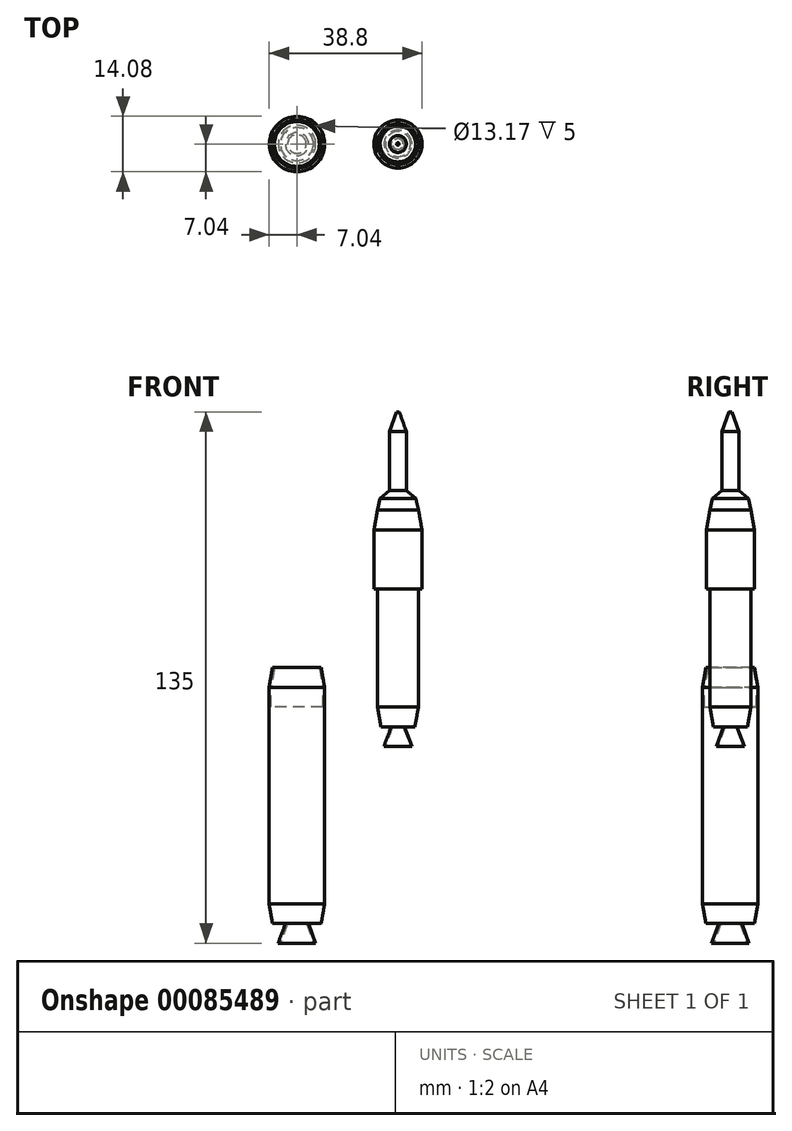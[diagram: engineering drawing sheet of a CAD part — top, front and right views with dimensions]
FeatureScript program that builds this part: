
annotation { "Feature Type Name" : "Feature", "Feature Type Description" : "" }
export const myFeature = defineFeature(function(context is Context, id is Id, definition is map)
    precondition{}
    {
        {
            var Q0;
            Q0=qCreatedBy(makeId("Top.planeOp"),FACE);
            var sketch = newSketch(context, id + "F0", { "sketchPlane" : qUnion([Q0])});
            skCircle(sketch, "E0", {"center": v(0, 0) * mm, "radius": 7.04 * mm});
            skSolve(sketch);
        }
        {
            var Q0;
            Q0=makeQuery(id+"F0.imprint","IMPRINT",FACE,{"disambiguationData":[TD([[makeQuery(id+"F0.imprint","IMPRINT",EDGE,{"derivedFrom":sQuery(id+"F0.wireOp",EDGE,"E0")}),1.0]])]});
            extrude(context, id + "F1", {"entities" : qUnion([Q0]), "depth" : 5 * mm, "hasSecondDirection" : true, "secondDirectionOppositeDirection" : true, "secondDirectionDepth" : 50 * mm});
        }
        {
            var Q0;
            Q0=makeQuery(id+"F1.opExtrude","CAP_FACE",FACE,{"disambiguationData":[OSD([sQuery(id+"F0.wireOp",EDGE,"E0")])],"isStart":true});
            extrude(context, id + "F2", {"entities" : qUnion([Q0]), "operationType" : NewBodyOperationType.ADD, "depth" : 5 * mm, "hasDraft" : true, "draftAngle" : 10 * degree, "draftPullDirection" : true});
        }
        {
            var Q0;
            Q0=makeQuery(id+"F1.opExtrude","CAP_FACE",FACE,{"disambiguationData":[OSD([sQuery(id+"F0.wireOp",EDGE,"E0")])],"isStart":false});
            extrude(context, id + "F3", {"entities" : qUnion([Q0]), "operationType" : NewBodyOperationType.ADD, "depth" : 5 * mm, "hasDraft" : true, "draftAngle" : 10 * degree, "draftPullDirection" : true});
        }
        {
            var Q0;
            Q0=makeQuery(id+"F3.opExtrude","CAP_FACE",FACE,{"disambiguationData":[OSD([sQuery(id+"F0.wireOp",EDGE,"E0")])],"isStart":false});
            var sketch = newSketch(context, id + "F4", { "sketchPlane" : qUnion([Q0])});
            skCircle(sketch, "E1", {"center": v(0, 0) * mm, "radius": 5.7 * mm});
            skSolve(sketch);
        }
        {
            var Q0;
            Q0 = qSketchRegion(id + "F4", true);
            extrude(context, id + "F5", {"entities" : qUnion([Q0]), "operationType" : NewBodyOperationType.REMOVE, "oppositeDirection" : true, "depth" : 5 * mm, "hasDraft" : true, "draftAngle" : 10 * degree});
        }
        {
            var Q0;
            Q0=makeQuery(id+"F2.opExtrude","CAP_FACE",FACE,{"disambiguationData":[OSD([sQuery(id+"F0.wireOp",EDGE,"E0")])],"isStart":false});
            var sketch = newSketch(context, id + "F6", { "sketchPlane" : qUnion([Q0])});
            skCircle(sketch, "E2", {"center": v(0, 0) * mm, "radius": 2.94 * mm});
            skSolve(sketch);
        }
        {
            var Q0;
            Q0 = qSketchRegion(id + "F6", true);
            extrude(context, id + "F7", {"entities" : qUnion([Q0]), "operationType" : NewBodyOperationType.ADD, "depth" : 5 * mm, "hasDraft" : true, "draftAngle" : 20 * degree});
        }
        {
            var Q0;
            Q0=makeQuery(id+"F7.opExtrude","CAP_FACE",FACE,{"disambiguationData":[OSD([sQuery(id+"F6.wireOp",EDGE,"E2")])],"isStart":false});
            var sketch = newSketch(context, id + "F8", { "sketchPlane" : qUnion([Q0])});
            skCircle(sketch, "E3", {"center": v(0, 0) * mm, "radius": 4.2 * mm});
            skSolve(sketch);
        }
        {
            var Q0;
            Q0 = qSketchRegion(id + "F8", true);
            extrude(context, id + "F9", {"entities" : qUnion([Q0]), "operationType" : NewBodyOperationType.REMOVE, "oppositeDirection" : true, "depth" : 5 * mm, "hasDraft" : true, "draftAngle" : 20 * degree, "draftPullDirection" : true});
        }
        {
            var Q0;
            Q0=qCreatedBy(makeId("Top.planeOp"),FACE);
            var sketch = newSketch(context, id + "F10", { "sketchPlane" : qUnion([Q0])});
            skCircle(sketch, "E4", {"center": v(25.65, 0) * mm, "radius": 5.21 * mm});
            skSolve(sketch);
        }
        {
            var Q0;
            Q0=makeQuery(id+"F10.imprint","IMPRINT",FACE,{"disambiguationData":[TD([[makeQuery(id+"F10.imprint","IMPRINT",EDGE,{"derivedFrom":sQuery(id+"F10.wireOp",EDGE,"E4")}),1.0]])]});
            extrude(context, id + "F11", {"entities" : qUnion([Q0]), "depth" : 30 * mm});
        }
        {
            var Q0;
            Q0=makeQuery(id+"F11.opExtrude","CAP_FACE",FACE,{"disambiguationData":[OSD([sQuery(id+"F10.wireOp",EDGE,"E4")])],"isStart":true});
            extrude(context, id + "F12", {"entities" : qUnion([Q0]), "operationType" : NewBodyOperationType.ADD, "depth" : 5 * mm, "hasDraft" : true, "draftAngle" : 10 * degree, "draftPullDirection" : true});
        }
        {
            var Q0;
            Q0=makeQuery(id+"F12.opExtrude","CAP_FACE",FACE,{"disambiguationData":[OSD([sQuery(id+"F10.wireOp",EDGE,"E4")])],"isStart":false});
            var sketch = newSketch(context, id + "F13", { "sketchPlane" : qUnion([Q0])});
            skCircle(sketch, "E5", {"center": v(25.65, 0) * mm, "radius": 1.72 * mm});
            skSolve(sketch);
        }
        {
            var Q0;
            Q0 = qSketchRegion(id + "F13", true);
            extrude(context, id + "F14", {"entities" : qUnion([Q0]), "operationType" : NewBodyOperationType.ADD, "depth" : 5 * mm, "hasDraft" : true, "draftAngle" : 20 * degree});
        }
        {
            var Q0;
            Q0=makeQuery(id+"F14.opExtrude","CAP_FACE",FACE,{"disambiguationData":[OSD([sQuery(id+"F13.wireOp",EDGE,"E5")])],"isStart":false});
            var sketch = newSketch(context, id + "F15", { "sketchPlane" : qUnion([Q0])});
            skCircle(sketch, "E6", {"center": v(25.65, 0) * mm, "radius": 3.17 * mm});
            skSolve(sketch);
        }
        {
            var Q0;
            Q0 = qSketchRegion(id + "F15", true);
            extrude(context, id + "F16", {"entities" : qUnion([Q0]), "operationType" : NewBodyOperationType.REMOVE, "oppositeDirection" : true, "depth" : 5 * mm, "hasDraft" : true, "draftAngle" : 20 * degree, "draftPullDirection" : true});
        }
        {
            var Q0;
            Q0=makeQuery(id+"F5.boolean.opBoolean","COPY",FACE,{"derivedFrom":makeQuery(id+"F5.opExtrude","CAP_FACE",FACE,{"disambiguationData":[OSD([sQuery(id+"F4.wireOp",EDGE,"E1")])],"isStart":false})});
            extrude(context, id + "F17", {"entities" : qUnion([Q0]), "operationType" : NewBodyOperationType.REMOVE, "oppositeDirection" : true, "depth" : 5 * mm});
        }
        {
            var Q0;
            Q0=makeQuery(id+"F11.opExtrude","CAP_FACE",FACE,{"disambiguationData":[OSD([sQuery(id+"F10.wireOp",EDGE,"E4")])],"isStart":false});
            var sketch = newSketch(context, id + "F18", { "sketchPlane" : qUnion([Q0])});
            skCircle(sketch, "E7", {"center": v(25.65, 0) * mm, "radius": 6.11 * mm});
            skSolve(sketch);
        }
        {
            var Q0;
            Q0 = qSketchRegion(id + "F18", true);
            extrude(context, id + "F19", {"entities" : qUnion([Q0]), "operationType" : NewBodyOperationType.ADD, "depth" : 15 * mm});
        }
        {
            var Q0;
            Q0=makeQuery(id+"F19.opExtrude","CAP_FACE",FACE,{"disambiguationData":[OSD([sQuery(id+"F18.wireOp",EDGE,"E7")])],"isStart":false});
            extrude(context, id + "F20", {"entities" : qUnion([Q0]), "operationType" : NewBodyOperationType.ADD, "depth" : 5 * mm, "hasDraft" : true, "draftAngle" : 10 * degree, "draftPullDirection" : true});
        }
        {
            var Q0;
            Q0=makeQuery(id+"F20.opExtrude","CAP_FACE",FACE,{"disambiguationData":[OSD([sQuery(id+"F18.wireOp",EDGE,"E7")])],"isStart":false});
            extrude(context, id + "F21", {"entities" : qUnion([Q0]), "operationType" : NewBodyOperationType.ADD, "depth" : 3 * mm, "hasDraft" : true, "draftAngle" : 13 * degree, "draftPullDirection" : true});
        }
        {
            var Q0;
            Q0=makeQuery(id+"F21.opExtrude","CAP_FACE",FACE,{"disambiguationData":[OSD([sQuery(id+"F18.wireOp",EDGE,"E7")])],"isStart":false});
            extrude(context, id + "F22", {"entities" : qUnion([Q0]), "operationType" : NewBodyOperationType.ADD, "depth" : 2 * mm, "hasDraft" : true, "draftAngle" : 50 * degree, "draftPullDirection" : true});
        }
        {
            var Q0;
            Q0=makeQuery(id+"F22.opExtrude","CAP_FACE",FACE,{"disambiguationData":[OSD([sQuery(id+"F18.wireOp",EDGE,"E7")])],"isStart":false});
            extrude(context, id + "F23", {"entities" : qUnion([Q0]), "operationType" : NewBodyOperationType.ADD, "depth" : 15 * mm});
        }
        {
            var Q0;
            Q0=makeQuery(id+"F23.opExtrude","CAP_FACE",FACE,{"disambiguationData":[OSD([sQuery(id+"F18.wireOp",EDGE,"E7")])],"isStart":false});
            extrude(context, id + "F24", {"entities" : qUnion([Q0]), "operationType" : NewBodyOperationType.ADD, "depth" : 5 * mm, "hasDraft" : true, "draftAngle" : 20 * degree, "draftPullDirection" : true});
        }
    });
